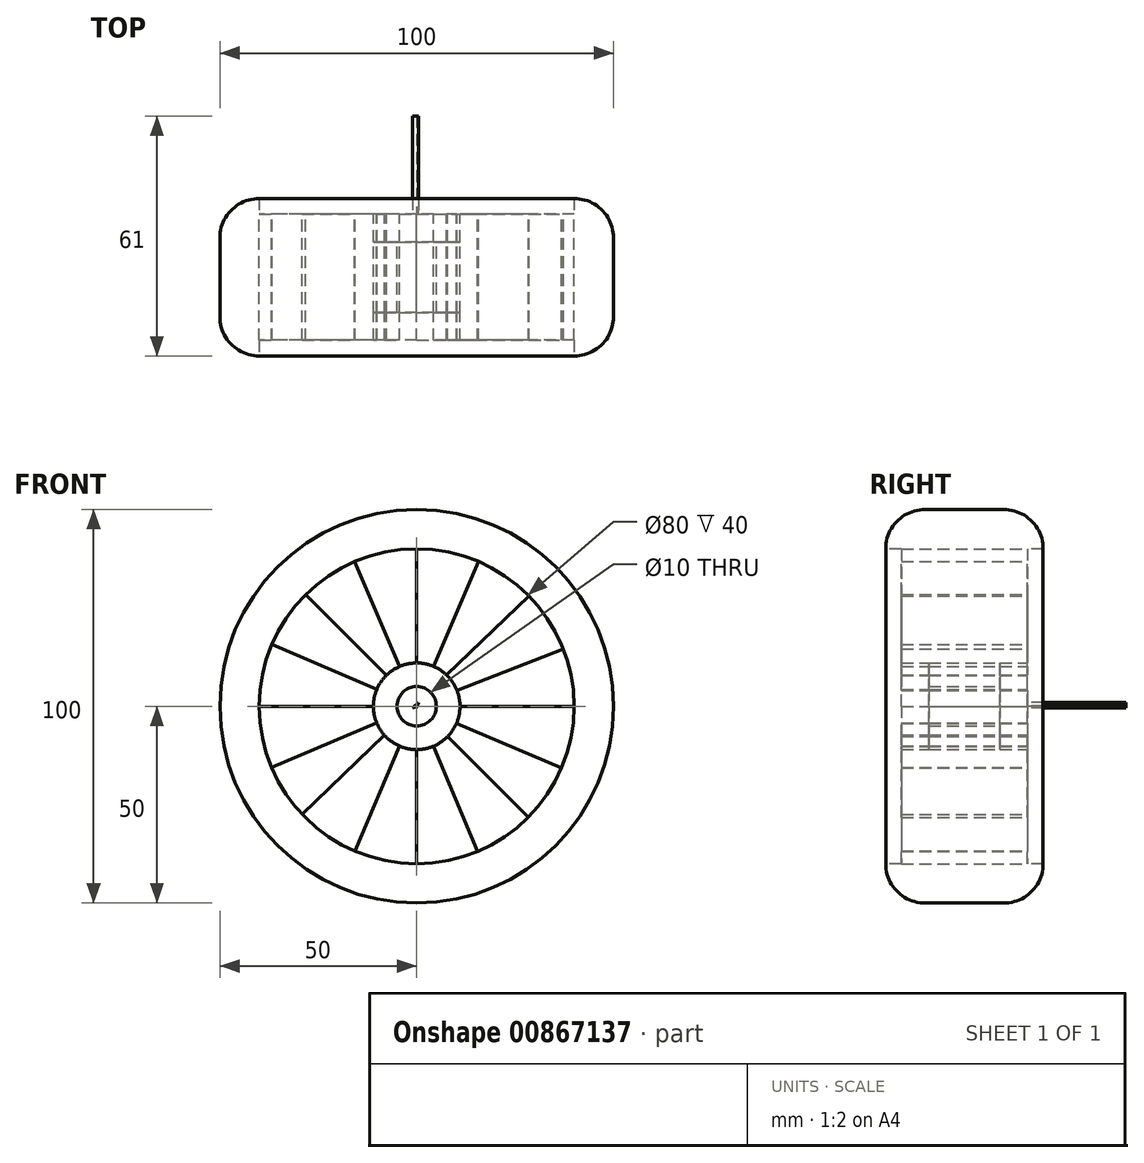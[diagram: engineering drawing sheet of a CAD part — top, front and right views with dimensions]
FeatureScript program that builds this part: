
annotation { "Feature Type Name" : "Feature", "Feature Type Description" : "" }
export const myFeature = defineFeature(function(context is Context, id is Id, definition is map)
    precondition{}
    {
        {
            var Q0;
            Q0=qCreatedBy(makeId("Front.planeOp"),FACE);
            var sketch = newSketch(context, id + "F0", { "sketchPlane" : qUnion([Q0])});
            skCircle(sketch, "E0", {"center": v(0, 0) * mm, "radius": 50 * mm});
            skSolve(sketch);
        }
        {
            var Q0;
            Q0=makeQuery(id+"F0.imprint","IMPRINT",FACE,{"disambiguationData":[TD([[makeQuery(id+"F0.imprint","IMPRINT",EDGE,{"derivedFrom":sQuery(id+"F0.wireOp",EDGE,"E0")}),1.0]])]});
            extrude(context, id + "F1", {"entities" : qUnion([Q0]), "depth" : 40 * mm, "offsetDistance" : 25 * mm});
        }
        {
            var Q0;
            Q0=makeQuery(id+"F1.opExtrude","CAP_FACE",FACE,{"disambiguationData":[OSD([sQuery(id+"F0.wireOp",EDGE,"E0")])],"isStart":false});
            var sketch = newSketch(context, id + "F2", { "sketchPlane" : qUnion([Q0])});
            skCircle(sketch, "E1", {"center": v(0, 0) * mm, "radius": 40 * mm});
            skSolve(sketch);
        }
        {
            var Q0;
            Q0=makeQuery(id+"F1.opExtrude","CAP_FACE",FACE,{"disambiguationData":[OSD([sQuery(id+"F0.wireOp",EDGE,"E0")])],"isStart":true});
            var Q1;
            Q1=makeQuery(id+"F1.opExtrude","SWEPT_FACE",FACE,{"disambiguationData":[OSD([sQuery(id+"F0.wireOp",EDGE,"E0")])]});
            fillet(context, id + "F3", {"entities" : qUnion([Q0, Q1]), "radius" : 10 * mm, "tangentPropagation" : true, "allowEdgeOverflow" : false});
        }
        {
            var Q0;
            Q0=makeQuery(id+"F2.imprint","IMPRINT",FACE,{"disambiguationData":[TD([[makeQuery(id+"F2.imprint","IMPRINT",EDGE,{"derivedFrom":sQuery(id+"F2.wireOp",EDGE,"E1")}),1.0]])]});
            extrude(context, id + "F4", {"entities" : qUnion([Q0]), "operationType" : NewBodyOperationType.REMOVE, "oppositeDirection" : true, "depth" : 4 * mm, "offsetDistance" : 25 * mm});
        }
        {
            var Q0;
            Q0=makeQuery(id+"F1.opExtrude","CAP_FACE",FACE,{"disambiguationData":[OSD([sQuery(id+"F0.wireOp",EDGE,"E0")])],"isStart":true});
            var sketch = newSketch(context, id + "F5", { "sketchPlane" : qUnion([Q0])});
            skCircle(sketch, "E2", {"center": v(0, 0) * mm, "radius": 40 * mm});
            skSolve(sketch);
        }
        {
            var Q0;
            Q0=makeQuery(id+"F5.imprint","IMPRINT",FACE,{"disambiguationData":[TD([[makeQuery(id+"F5.imprint","IMPRINT",EDGE,{"derivedFrom":sQuery(id+"F5.wireOp",EDGE,"E2")}),1.0]])]});
            extrude(context, id + "F6", {"entities" : qUnion([Q0]), "operationType" : NewBodyOperationType.REMOVE, "oppositeDirection" : true, "depth" : 4 * mm, "offsetDistance" : 25 * mm});
        }
        {
            var Q0;
            Q0=makeQuery(id+"F6.boolean.opBoolean","COPY",FACE,{"derivedFrom":makeQuery(id+"F6.opExtrude","CAP_FACE",FACE,{"disambiguationData":[OSD([sQuery(id+"F5.wireOp",EDGE,"E2")])],"isStart":false})});
            var sketch = newSketch(context, id + "F7", { "sketchPlane" : qUnion([Q0])});
            skCircle(sketch, "E3", {"center": v(0, 0) * mm, "radius": 11 * mm});
            skCircle(sketch, "E4", {"center": v(0, 0) * mm, "radius": 11.17 * mm});
            skSolve(sketch);
        }
        {
            var Q0;
            Q0=makeQuery(id+"F7.imprint","IMPRINT",FACE,{"disambiguationData":[TD([[makeQuery(id+"F7.imprint","IMPRINT",EDGE,{"derivedFrom":sQuery(id+"F7.wireOp",EDGE,"E3")}),1.0]])]});
            extrude(context, id + "F8", {"entities" : qUnion([Q0]), "operationType" : NewBodyOperationType.REMOVE, "oppositeDirection" : true, "depth" : 7 * mm, "offsetDistance" : 25 * mm});
        }
        {
            var Q0;
            Q0=makeQuery(id+"F4.boolean.opBoolean","COPY",FACE,{"derivedFrom":makeQuery(id+"F4.opExtrude","CAP_FACE",FACE,{"disambiguationData":[OSD([sQuery(id+"F2.wireOp",EDGE,"E1")])],"isStart":false})});
            var sketch = newSketch(context, id + "F9", { "sketchPlane" : qUnion([Q0])});
            skCircle(sketch, "E5", {"center": v(0, 0) * mm, "radius": 11 * mm});
            skSolve(sketch);
        }
        {
            var Q0;
            Q0=makeQuery(id+"F9.imprint","IMPRINT",FACE,{"disambiguationData":[TD([[makeQuery(id+"F9.imprint","IMPRINT",EDGE,{"derivedFrom":sQuery(id+"F9.wireOp",EDGE,"E5")}),1.0]])]});
            extrude(context, id + "F10", {"entities" : qUnion([Q0]), "operationType" : NewBodyOperationType.REMOVE, "oppositeDirection" : true, "depth" : 7 * mm, "offsetDistance" : 25 * mm});
        }
        {
            var Q0;
            Q0=makeQuery(id+"F6.boolean.opBoolean","COPY",FACE,{"derivedFrom":makeQuery(id+"F6.opExtrude","CAP_FACE",FACE,{"disambiguationData":[OSD([sQuery(id+"F5.wireOp",EDGE,"E2")])],"isStart":false})});
            var sketch = newSketch(context, id + "F11", { "sketchPlane" : qUnion([Q0])});
            skPoint(sketch, "E6", {"position": v(0, 0) * mm});
            skSolve(sketch);
        }
        {
            var Q0;
            Q0=sQuery(id+"F11.wireOp",VERTEX,"E6");
            var Q1;
            Q1=makeQuery(id+"F1.opExtrude","SWEPT_BODY",BODY,{"disambiguationData":[OSD([sQuery(id+"F0.wireOp",EDGE,"E0")])]});
            hole(context, id + "F12", {"style" : HoleStyle.SIMPLE, "endStyle" : HoleEndStyle.THROUGH, "holeDiameter" : 10 * mm, "majorDiameter" : 5 * mm, "isTappedThrough" : true, "tappedDepth" : 12 * mm, "tapClearance" : 3, "startFromSketch" : true, "locations" : qUnion([Q0]), "scope" : qUnion([Q1])});
        }
        {
            var Q0;
            Q0=makeQuery(id+"F6.boolean.opBoolean","COPY",FACE,{"derivedFrom":makeQuery(id+"F6.opExtrude","CAP_FACE",FACE,{"disambiguationData":[OSD([sQuery(id+"F5.wireOp",EDGE,"E2")])],"isStart":false})});
            var sketch = newSketch(context, id + "F13", { "sketchPlane" : qUnion([Q0])});
            skLineSegment(sketch, "E7", {"start": v(0, 0) * mm, "end": v(-36.79, -15.7) * mm});
            skLineSegment(sketch, "E8", {"start": v(0, 0) * mm, "end": v(-15.48, -36.88) * mm});
            skLineSegment(sketch, "E9", {"start": v(0, 0) * mm, "end": v(15.7, -36.79) * mm});
            skLineSegment(sketch, "E10", {"start": v(0, 0) * mm, "end": v(36.88, -15.48) * mm});
            skLineSegment(sketch, "E11", {"start": v(0, 0) * mm, "end": v(-37.27, 14.53) * mm});
            skLineSegment(sketch, "E12", {"start": v(0, 0) * mm, "end": v(15.74, 36.77) * mm});
            skLineSegment(sketch, "E13", {"start": v(0, 0) * mm, "end": v(-15.7, 36.79) * mm});
            skLineSegment(sketch, "E14", {"start": v(0, 0) * mm, "end": v(36.79, 15.7) * mm});
            skLineSegment(sketch, "E15", {"start": v(-28.54, 28.02) * mm, "end": v(29.12, -27.42) * mm});
            skLineSegment(sketch, "E16", {"start": v(-28.37, -28.2) * mm, "end": v(28.18, 28.38) * mm});
            skLineSegment(sketch, "E17", {"start": v(-40, 0) * mm, "end": v(40, 0) * mm});
            skLineSegment(sketch, "E18", {"start": v(0, 40) * mm, "end": v(0, -40) * mm});
            skSolve(sketch);
        }
        {
            var Q0;
            Q0 = qSketchRegion(id + "F13", true);
            extrude(context, id + "F14", {"entities" : qUnion([Q0]), "depth" : 25 * mm, "offsetDistance" : 25 * mm});
        }
        {
            var Q0;
            {var subQ0=sQuery(id+"F13.wireOp",EDGE,"E11");var subQ1=makeQuery(id+"F6.boolean.opBoolean","COPY",EDGE,{"derivedFrom":makeQuery(id+"F6.opExtrude","CAP_EDGE",EDGE,{"disambiguationData":[OSD([sQuery(id+"F5.wireOp",EDGE,"E2")])],"isStart":false})});var subQ2=makeQuery(id+"F13.imprint","INTERSECT",VERTEX,{"derivedFrom":[subQ1,subQ0]});Q0=makeQuery(id+"F13.imprint","IMPRINT",FACE,{"disambiguationData":[TD([[makeQuery(id+"F13.imprint","IMPRINT",EDGE,{"disambiguationData":[TD([[subQ2,1.0]])],"derivedFrom":subQ0}),-1.0]])]});}
            var sketch = newSketch(context, id + "F15", { "sketchPlane" : qUnion([Q0])});
            skSolve(sketch);
        }
        {
            var Q0;
            {var subQ0=sQuery(id+"F13.wireOp",EDGE,"E11");var subQ1=makeQuery(id+"F6.boolean.opBoolean","COPY",EDGE,{"derivedFrom":makeQuery(id+"F6.opExtrude","CAP_EDGE",EDGE,{"disambiguationData":[OSD([sQuery(id+"F5.wireOp",EDGE,"E2")])],"isStart":false})});var subQ2=makeQuery(id+"F13.imprint","INTERSECT",VERTEX,{"derivedFrom":[subQ1,subQ0]});Q0=makeQuery(id+"F15.imprint","IMPRINT",FACE,{"disambiguationData":[TD([[makeQuery(id+"F15.imprint","IMPRINT",EDGE,{"derivedFrom":makeQuery(id+"F13.imprint","IMPRINT",EDGE,{"disambiguationData":[TD([[subQ2,1.0]])],"derivedFrom":subQ0})}),-1.0]])]});}
            var Q1;
            {var subQ0=sQuery(id+"F13.wireOp",EDGE,"E7");var subQ1=makeQuery(id+"F6.boolean.opBoolean","COPY",EDGE,{"derivedFrom":makeQuery(id+"F6.opExtrude","CAP_EDGE",EDGE,{"disambiguationData":[OSD([sQuery(id+"F5.wireOp",EDGE,"E2")])],"isStart":false})});var subQ2=makeQuery(id+"F13.imprint","INTERSECT",VERTEX,{"derivedFrom":[subQ1,subQ0]});Q1=makeQuery(id+"F13.imprint","IMPRINT",FACE,{"disambiguationData":[TD([[makeQuery(id+"F13.imprint","IMPRINT",EDGE,{"disambiguationData":[TD([[subQ2,1.0]])],"derivedFrom":subQ0}),-1.0]])]});}
            var Q2;
            {var subQ0=sQuery(id+"F13.wireOp",EDGE,"E8");var subQ1=makeQuery(id+"F6.boolean.opBoolean","COPY",EDGE,{"derivedFrom":makeQuery(id+"F6.opExtrude","CAP_EDGE",EDGE,{"disambiguationData":[OSD([sQuery(id+"F5.wireOp",EDGE,"E2")])],"isStart":false})});var subQ2=makeQuery(id+"F13.imprint","INTERSECT",VERTEX,{"derivedFrom":[subQ1,subQ0]});Q2=makeQuery(id+"F13.imprint","IMPRINT",FACE,{"disambiguationData":[TD([[makeQuery(id+"F13.imprint","IMPRINT",EDGE,{"disambiguationData":[TD([[subQ2,1.0]])],"derivedFrom":subQ0}),-1.0]])]});}
            var Q3;
            {var subQ0=sQuery(id+"F13.wireOp",EDGE,"E9");var subQ1=makeQuery(id+"F6.boolean.opBoolean","COPY",EDGE,{"derivedFrom":makeQuery(id+"F6.opExtrude","CAP_EDGE",EDGE,{"disambiguationData":[OSD([sQuery(id+"F5.wireOp",EDGE,"E2")])],"isStart":false})});var subQ2=makeQuery(id+"F13.imprint","INTERSECT",VERTEX,{"derivedFrom":[subQ1,subQ0]});Q3=makeQuery(id+"F13.imprint","IMPRINT",FACE,{"disambiguationData":[TD([[makeQuery(id+"F13.imprint","IMPRINT",EDGE,{"disambiguationData":[TD([[subQ2,1.0]])],"derivedFrom":subQ0}),-1.0]])]});}
            var Q4;
            {var subQ0=sQuery(id+"F13.wireOp",EDGE,"E10");var subQ1=makeQuery(id+"F6.boolean.opBoolean","COPY",EDGE,{"derivedFrom":makeQuery(id+"F6.opExtrude","CAP_EDGE",EDGE,{"disambiguationData":[OSD([sQuery(id+"F5.wireOp",EDGE,"E2")])],"isStart":false})});var subQ2=makeQuery(id+"F13.imprint","INTERSECT",VERTEX,{"derivedFrom":[subQ1,subQ0]});Q4=makeQuery(id+"F13.imprint","IMPRINT",FACE,{"disambiguationData":[TD([[makeQuery(id+"F13.imprint","IMPRINT",EDGE,{"disambiguationData":[TD([[subQ2,1.0]])],"derivedFrom":subQ0}),-1.0]])]});}
            var Q5;
            {var subQ0=sQuery(id+"F13.wireOp",EDGE,"E14");var subQ1=makeQuery(id+"F6.boolean.opBoolean","COPY",EDGE,{"derivedFrom":makeQuery(id+"F6.opExtrude","CAP_EDGE",EDGE,{"disambiguationData":[OSD([sQuery(id+"F5.wireOp",EDGE,"E2")])],"isStart":false})});var subQ2=makeQuery(id+"F13.imprint","INTERSECT",VERTEX,{"derivedFrom":[subQ1,subQ0]});Q5=makeQuery(id+"F13.imprint","IMPRINT",FACE,{"disambiguationData":[TD([[makeQuery(id+"F13.imprint","IMPRINT",EDGE,{"disambiguationData":[TD([[subQ2,1.0]])],"derivedFrom":subQ0}),-1.0]])]});}
            var Q6;
            {var subQ0=sQuery(id+"F13.wireOp",EDGE,"E12");var subQ1=makeQuery(id+"F6.boolean.opBoolean","COPY",EDGE,{"derivedFrom":makeQuery(id+"F6.opExtrude","CAP_EDGE",EDGE,{"disambiguationData":[OSD([sQuery(id+"F5.wireOp",EDGE,"E2")])],"isStart":false})});var subQ2=makeQuery(id+"F13.imprint","INTERSECT",VERTEX,{"derivedFrom":[subQ1,subQ0]});Q6=makeQuery(id+"F13.imprint","IMPRINT",FACE,{"disambiguationData":[TD([[makeQuery(id+"F13.imprint","IMPRINT",EDGE,{"disambiguationData":[TD([[subQ2,1.0]])],"derivedFrom":subQ0}),-1.0]])]});}
            var Q7;
            {var subQ0=sQuery(id+"F13.wireOp",EDGE,"E13");var subQ1=makeQuery(id+"F6.boolean.opBoolean","COPY",EDGE,{"derivedFrom":makeQuery(id+"F6.opExtrude","CAP_EDGE",EDGE,{"disambiguationData":[OSD([sQuery(id+"F5.wireOp",EDGE,"E2")])],"isStart":false})});var subQ2=makeQuery(id+"F13.imprint","INTERSECT",VERTEX,{"derivedFrom":[subQ1,subQ0]});Q7=makeQuery(id+"F13.imprint","IMPRINT",FACE,{"disambiguationData":[TD([[makeQuery(id+"F13.imprint","IMPRINT",EDGE,{"disambiguationData":[TD([[subQ2,1.0]])],"derivedFrom":subQ0}),-1.0]])]});}
            extrude(context, id + "F16", {"entities" : qUnion([Q0, Q1, Q2, Q3, Q4, Q5, Q6, Q7]), "operationType" : NewBodyOperationType.REMOVE, "endBound" : BoundingType.UP_TO_NEXT, "oppositeDirection" : true, "depth" : 25 * mm, "offsetDistance" : 25 * mm});
        }
    });
